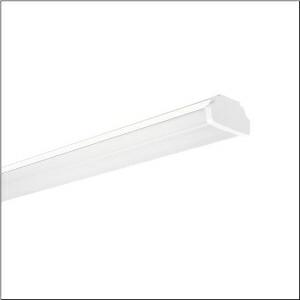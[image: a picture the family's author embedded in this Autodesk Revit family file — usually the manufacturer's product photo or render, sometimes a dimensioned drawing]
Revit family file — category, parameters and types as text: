
# Revit family: modario_r__31_mo_53bm812d2v6085_42f2
name_source: partatom
category: Lighting Fixtures
units: mm (PartAtom-declared; Revit-internal decimal feet)

## family parameters
Cut with Voids When Loaded = No
Host = Face
Light Source = No
Part Type = Normal
Room Calculation Point = No
Round Connector Dimension = Use Diameter
Shared = No

## types (1)
- --- (1 x LED, 8960 lm, 61.8 W, 6500K)
    Apparent Load = 62 VA
    CIE Flux Codes = 47 80 95 92 100
    Color Rendering = 80
    Color Temperature = 6500K
    Default Elevation = 1800 mm
    Description = Modario® 31 MOluminaire insert, length: 1.495mm, width: 81mm, height: 82mm, LED rated luminous flux: 8.960lm, light colour: 865, control gear: DALI 2, control gear: ECG DALI, with plug, 5-pole, with phase selection, mains connection: 220..240V, AC, 50/60Hz, primary optical cover: cover, of PMMA, light emission: direct distribution, primary light characteristic: symmetric, protection rating (complete): IP20, protection rating (LED compartment): IP50, insulation class (complete): insulation class I (protective earthing), certification: CE, ENEC, VDE, permissible ambient temperature for indoor applications: -25..+30°C, corresponds to IFS (International Featured Standards) requirements for safety and quality in the food industry, reducing of maximum allowable ambient temperature of 5°C with ceiling mounting, packaging unit: 1 piece
    Height = 92 mm
    Lamp = 1 x LED
    Lamp Light Flux = 8960 lm
    Lamp Power = 61.8 W
    Lamp count = 1
    Length = 1495 mm
    Luminous efficacy = 145 lm/W
    Manufacturer = Siteco
    ModVariant = No
    Model = 53BM812D2V6085
    Mounting Place = Ceiling
    Mounting Type = Pendant
    Number of Poles = 1
    OnlyDefault = Yes
    Power Factor = 1
    Product Name = Modario® 31 MO
    Product group = luminaire insert
    ProductGroupID = 902
    Protection Class = Protection class I
    Protection Degree = IP 20
    RLX_Detail_Level = 1
    RlxData = <blob elided: 42249 chars, md5=bc6c1e62>
    Socket = socket
    Standby Power = 0 W
    System Light Flux = 8960 lm
    System Power = 62 W
    Type Comments = factory setting: luminous flux: 100 % | dim-lin: 254 | 500 mA
    Type Image = l_1003447.jpg
    URL = http://relux.com
    VarID = @adj_117375
    Voltage = 0 V
    Weight = 0.00 kg
    Width = 81 mm

## geometry (parser evidence)
native form markers: Blend x4, Sweep x12
no freeform markers — native parametric forms only
